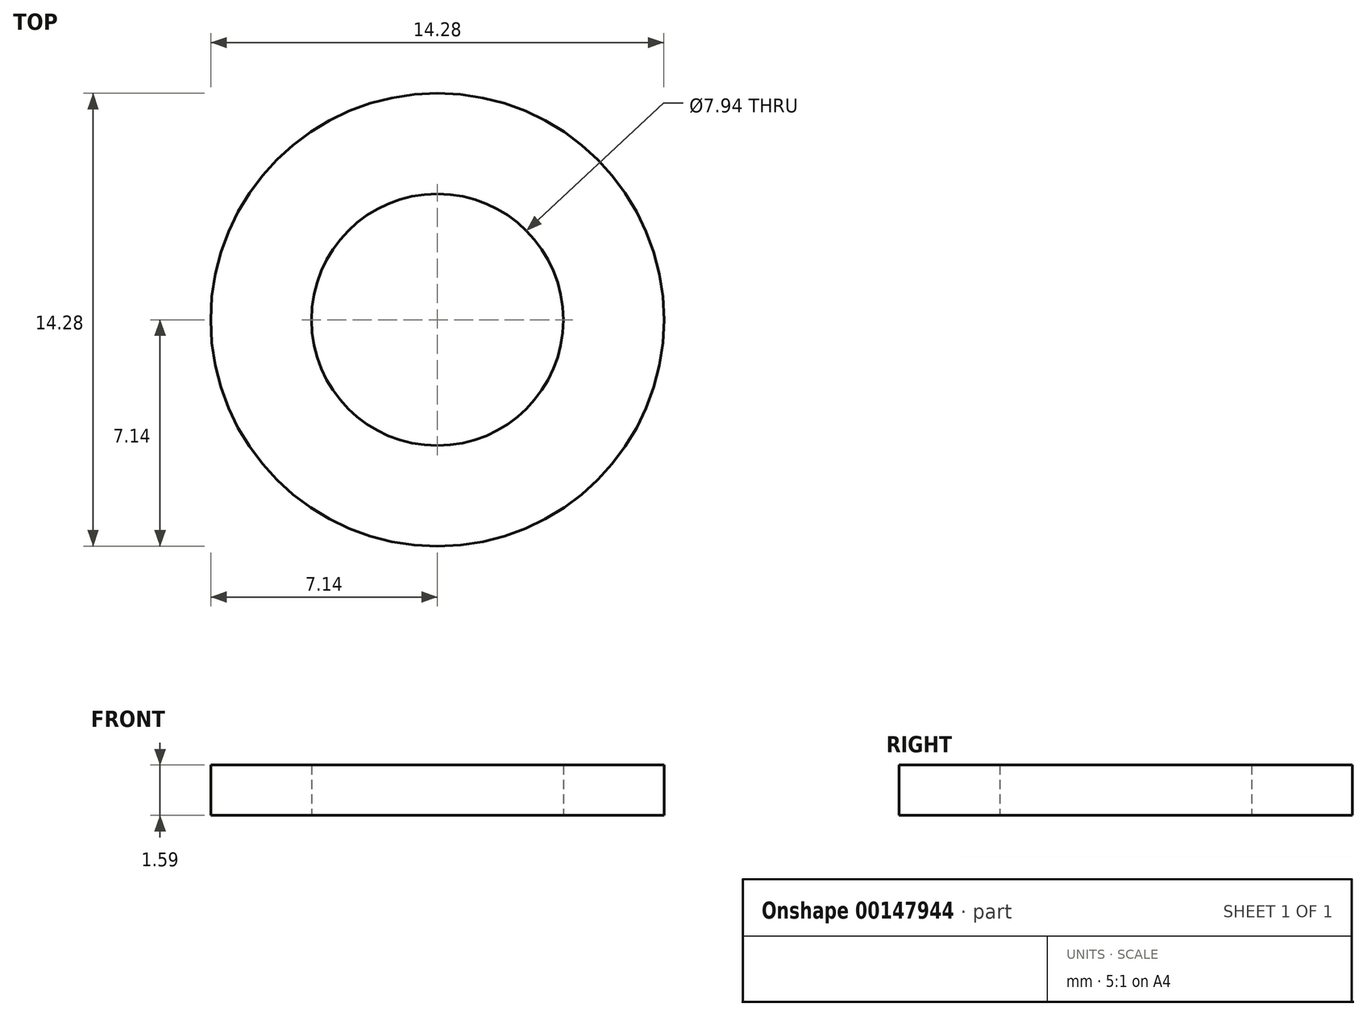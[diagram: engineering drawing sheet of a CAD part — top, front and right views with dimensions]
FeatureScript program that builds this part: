
annotation { "Feature Type Name" : "Feature", "Feature Type Description" : "" }
export const myFeature = defineFeature(function(context is Context, id is Id, definition is map)
    precondition{}
    {
        {
            var Q0;
            Q0=qCreatedBy(makeId("Top.planeOp"),FACE);
            var sketch = newSketch(context, id + "F0", { "sketchPlane" : qUnion([Q0])});
            skCircle(sketch, "E0", {"center": v(0, 0) * mm, "radius": 3.97 * mm});
            skCircle(sketch, "E1", {"center": v(0, 0) * mm, "radius": 7.14 * mm});
            skSolve(sketch);
        }
        {
            var Q0;
            Q0=qSketchRegion(id+"F0",true);
            extrude(context, id + "F1", {"entities" : qUnion([Q0]), "depth" : 1.59 * mm});
        }
    });
